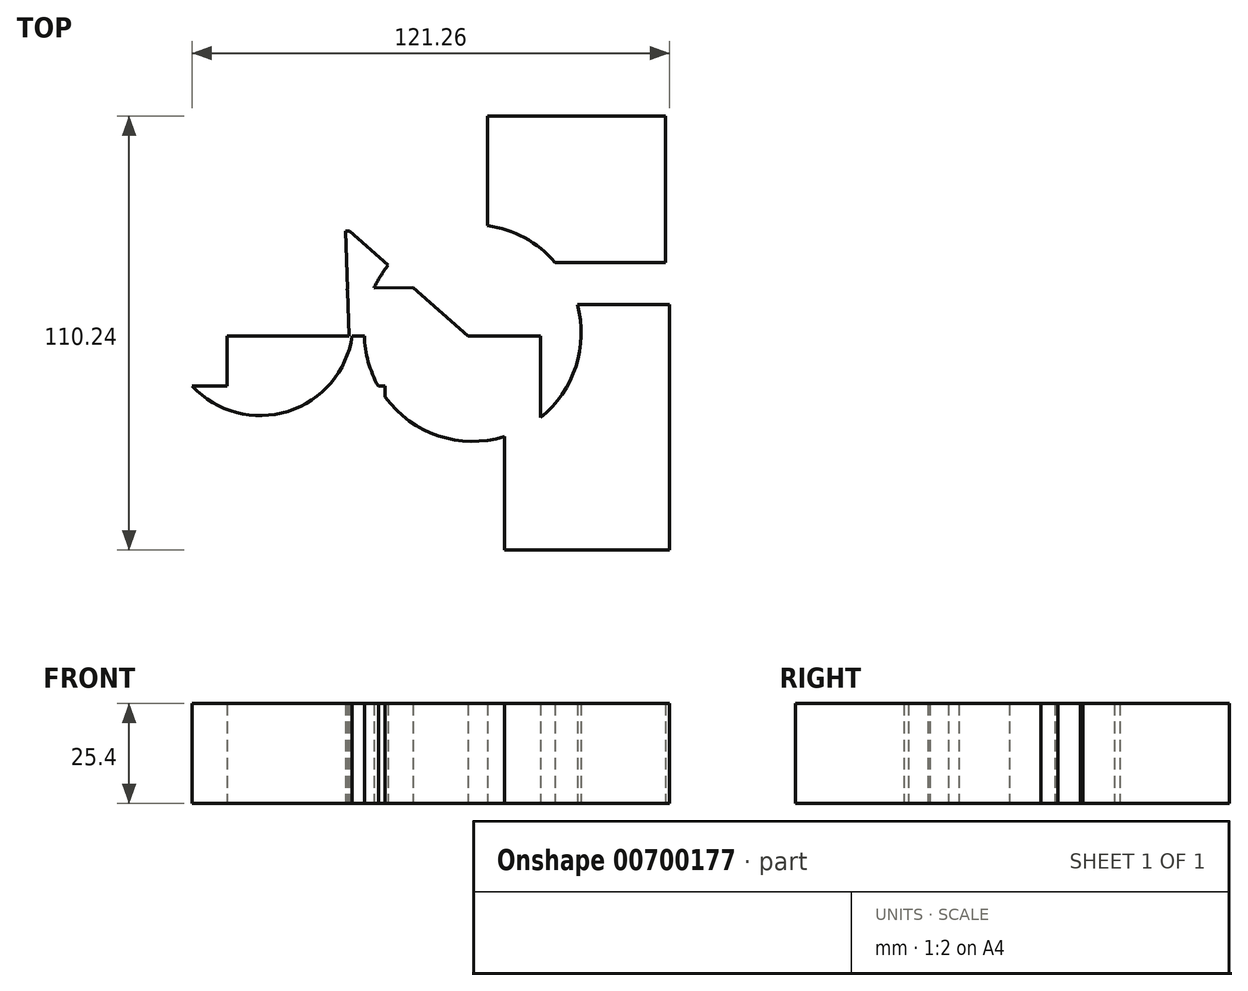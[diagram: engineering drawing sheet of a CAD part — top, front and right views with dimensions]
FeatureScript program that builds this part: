
annotation { "Feature Type Name" : "Feature", "Feature Type Description" : "" }
export const myFeature = defineFeature(function(context is Context, id is Id, definition is map)
    precondition{}
    {
        {
            var Q0;
            Q0=qCreatedBy(makeId("Top.planeOp"),FACE);
            var sketch = newSketch(context, id + "F0", { "sketchPlane" : qUnion([Q0])});
            skLineSegment(sketch, "E0.bottom", {"start": v(-22.83, 32.45) * mm, "end": v(-5.78, 32.45) * mm});
            skLineSegment(sketch, "E0.right", {"start": v(-5.78, 32.45) * mm, "end": v(-5.78, 62.5) * mm});
            skArc(sketch, "E1", {"start": v(30.4, 24.45) * mm, "mid": v(-14.8, -6.45) * mm, "end": v(36.07, 13.78) * mm});
            skLineSegment(sketch, "E2.bottom", {"start": v(17.51, -48.63) * mm, "end": v(59.47, -48.63) * mm});
            skLineSegment(sketch, "E2.top", {"start": v(36.07, 13.78) * mm, "end": v(59.47, 13.78) * mm});
            skLineSegment(sketch, "E2.left", {"start": v(17.51, -48.63) * mm, "end": v(17.51, -19.86) * mm});
            skLineSegment(sketch, "E2.right", {"start": v(59.47, -48.63) * mm, "end": v(59.47, 13.78) * mm});
            skLineSegment(sketch, "E3", {"start": v(-22.83, 32.45) * mm, "end": v(-21.42, -11.3) * mm});
            skLineSegment(sketch, "E4", {"start": v(-39.2, 50.05) * mm, "end": v(-5.78, 47.18) * mm});
            skArc(sketch, "E5", {"start": v(-62.4, -6.35) * mm, "mid": v(-25.36, -4.68) * mm, "end": v(-35.45, 31) * mm});
            skLineSegment(sketch, "E6.bottom", {"start": v(58.4, 61.6) * mm, "end": v(13.25, 61.6) * mm});
            skLineSegment(sketch, "E6.top", {"start": v(58.4, 24.45) * mm, "end": v(30.4, 24.45) * mm});
            skLineSegment(sketch, "E6.left", {"start": v(58.4, 61.6) * mm, "end": v(58.4, 24.45) * mm});
            skLineSegment(sketch, "E6.right", {"start": v(13.25, 61.6) * mm, "end": v(13.25, 24.45) * mm});
            skLineSegment(sketch, "E7.trimOffspring", {"start": v(13.25, 45.54) * mm, "end": v(35.3, 43.65) * mm});
            skLineSegment(sketch, "E8.bottom", {"start": v(-63.74, -55.92) * mm, "end": v(-12.71, -55.92) * mm});
            skLineSegment(sketch, "E8.top", {"start": v(-63.74, -7.02) * mm, "end": v(-12.71, -7.02) * mm});
            skLineSegment(sketch, "E8.left", {"start": v(-63.74, -55.92) * mm, "end": v(-63.74, -7.02) * mm});
            skLineSegment(sketch, "E8.right", {"start": v(-12.71, -9.77) * mm, "end": v(-12.71, -7.02) * mm});
            skLineSegment(sketch, "E9.bottom", {"start": v(-52.9, -38.5) * mm, "end": v(26.76, -38.5) * mm});
            skLineSegment(sketch, "E9.top", {"start": v(-52.9, 5.78) * mm, "end": v(26.76, 5.78) * mm});
            skLineSegment(sketch, "E9.left", {"start": v(-52.9, -38.5) * mm, "end": v(-52.9, 5.78) * mm});
            skLineSegment(sketch, "E9.right", {"start": v(26.76, -38.5) * mm, "end": v(26.76, 5.78) * mm});
            skLineSegment(sketch, "E10", {"start": v(-50.05, 57.52) * mm, "end": v(47.56, -29.07) * mm});
            skLineSegment(sketch, "E11", {"start": v(47.2, 19.3) * mm, "end": v(-54.85, 16.98) * mm});
            skSolve(sketch);
        }
        {
            var Q0;
            {var subQ1=sQuery(id+"F0.wireOp",EDGE,"E6.bottom");Q0=makeQuery(id+"F0.imprint","IMPRINT",FACE,{"disambiguationData":[TD([[makeQuery(id+"F0.imprint","IMPRINT",EDGE,{"derivedFrom":subQ1}),1.0]])]});}
            var Q1;
            {var subQ0=sQuery(id+"F0.wireOp",EDGE,"E11");var subQ1=sQuery(id+"F0.wireOp",EDGE,"E3");var subQ2=makeQuery(id+"F0.imprint","INTERSECT",VERTEX,{"derivedFrom":[subQ1,subQ0]});Q1=makeQuery(id+"F0.imprint","IMPRINT",FACE,{"disambiguationData":[TD([[makeQuery(id+"F0.imprint","IMPRINT",EDGE,{"disambiguationData":[TD([[subQ2,-1.0]])],"derivedFrom":subQ1}),-1.0]])]});}
            var Q2;
            {var subQ0=sQuery(id+"F0.wireOp",EDGE,"E8.top");var subQ1=sQuery(id+"F0.wireOp",EDGE,"E5");var subQ2=makeQuery(id+"F0.imprint","INTERSECT",VERTEX,{"disambiguationData":[OD(0.0)],"derivedFrom":[subQ1,subQ0]});Q2=makeQuery(id+"F0.imprint","IMPRINT",FACE,{"disambiguationData":[TD([[makeQuery(id+"F0.imprint","IMPRINT",EDGE,{"disambiguationData":[TD([[subQ2,-1.0]])],"derivedFrom":subQ1}),1.0]])]});}
            var Q3;
            {var subQ0=sQuery(id+"F0.wireOp",EDGE,"E9.right");var subQ1=sQuery(id+"F0.wireOp",EDGE,"E9.top");var subQ2=makeQuery(id+"F0.imprint","INTERSECT",VERTEX,{"derivedFrom":[subQ1,subQ0]});Q3=makeQuery(id+"F0.imprint","IMPRINT",FACE,{"disambiguationData":[TD([[makeQuery(id+"F0.imprint","IMPRINT",EDGE,{"disambiguationData":[TD([[subQ2,1.0]])],"derivedFrom":subQ1}),-1.0]])]});}
            var Q4;
            {var subQ5=sQuery(id+"F0.wireOp",EDGE,"E0.bottom");var subQ7=sQuery(id+"F0.wireOp",EDGE,"E3");var subQ8=makeQuery(id+"F0.imprint","INTERSECT",VERTEX,{"derivedFrom":[subQ5,subQ7]});Q4=makeQuery(id+"F0.imprint","IMPRINT",FACE,{"disambiguationData":[TD([[makeQuery(id+"F0.imprint","IMPRINT",EDGE,{"disambiguationData":[TD([[subQ8,-1.0]])],"derivedFrom":subQ5}),-1.0]])]});}
            var Q5;
            {var subQ0=sQuery(id+"F0.wireOp",EDGE,"E10");var subQ1=sQuery(id+"F0.wireOp",EDGE,"E1");var subQ2=makeQuery(id+"F0.imprint","INTERSECT",VERTEX,{"disambiguationData":[OD(0.0)],"derivedFrom":[subQ1,subQ0]});Q5=makeQuery(id+"F0.imprint","IMPRINT",FACE,{"disambiguationData":[TD([[makeQuery(id+"F0.imprint","IMPRINT",EDGE,{"disambiguationData":[TD([[subQ2,-1.0]])],"derivedFrom":subQ1}),1.0]])]});}
            var Q6;
            {var subQ1=sQuery(id+"F0.wireOp",EDGE,"E2.bottom");Q6=makeQuery(id+"F0.imprint","IMPRINT",FACE,{"disambiguationData":[TD([[makeQuery(id+"F0.imprint","IMPRINT",EDGE,{"derivedFrom":subQ1}),1.0]])]});}
            var Q7;
            {var subQ0=sQuery(id+"F0.wireOp",EDGE,"E10");var subQ1=sQuery(id+"F0.wireOp",EDGE,"E1");var subQ2=makeQuery(id+"F0.imprint","INTERSECT",VERTEX,{"disambiguationData":[OD(1.0)],"derivedFrom":[subQ1,subQ0]});Q7=makeQuery(id+"F0.imprint","IMPRINT",FACE,{"disambiguationData":[TD([[makeQuery(id+"F0.imprint","IMPRINT",EDGE,{"disambiguationData":[TD([[subQ2,1.0]])],"derivedFrom":subQ1}),1.0]])]});}
            var Q8;
            {var subQ0=sQuery(id+"F0.wireOp",EDGE,"E5");var subQ1=sQuery(id+"F0.wireOp",EDGE,"E3");var subQ2=makeQuery(id+"F0.imprint","INTERSECT",VERTEX,{"disambiguationData":[OD(0.0)],"derivedFrom":[subQ1,subQ0]});Q8=makeQuery(id+"F0.imprint","IMPRINT",FACE,{"disambiguationData":[TD([[makeQuery(id+"F0.imprint","IMPRINT",EDGE,{"disambiguationData":[TD([[subQ2,-1.0]])],"derivedFrom":subQ1}),1.0]])]});}
            var Q9;
            {var subQ0=sQuery(id+"F0.wireOp",EDGE,"E11");var subQ1=sQuery(id+"F0.wireOp",EDGE,"E1");var subQ2=makeQuery(id+"F0.imprint","INTERSECT",VERTEX,{"derivedFrom":[subQ1,subQ0]});Q9=makeQuery(id+"F0.imprint","IMPRINT",FACE,{"disambiguationData":[TD([[makeQuery(id+"F0.imprint","IMPRINT",EDGE,{"disambiguationData":[TD([[subQ2,-1.0]])],"derivedFrom":subQ1}),1.0]])]});}
            var Q10;
            {var subQ0=sQuery(id+"F0.wireOp",EDGE,"E2.left");var subQ1=sQuery(id+"F0.wireOp",EDGE,"E1");var subQ2=makeQuery(id+"F0.imprint","INTERSECT",VERTEX,{"derivedFrom":[subQ1,subQ0]});Q10=makeQuery(id+"F0.imprint","IMPRINT",FACE,{"disambiguationData":[TD([[makeQuery(id+"F0.imprint","IMPRINT",EDGE,{"disambiguationData":[TD([[subQ2,-1.0]])],"derivedFrom":subQ1}),-1.0]])]});}
            var Q11;
            {var subQ1=sQuery(id+"F0.wireOp",EDGE,"E9.top");var subQ3=sQuery(id+"F0.wireOp",EDGE,"E3");var subQ4=makeQuery(id+"F0.imprint","INTERSECT",VERTEX,{"derivedFrom":[subQ3,subQ1]});Q11=makeQuery(id+"F0.imprint","IMPRINT",FACE,{"disambiguationData":[TD([[makeQuery(id+"F0.imprint","IMPRINT",EDGE,{"disambiguationData":[TD([[subQ4,-1.0]])],"derivedFrom":subQ3}),-1.0]])]});}
            var Q12;
            {var subQ0=sQuery(id+"F0.wireOp",EDGE,"E9.top");var subQ1=sQuery(id+"F0.wireOp",EDGE,"E3");var subQ2=makeQuery(id+"F0.imprint","INTERSECT",VERTEX,{"derivedFrom":[subQ1,subQ0]});Q12=makeQuery(id+"F0.imprint","IMPRINT",FACE,{"disambiguationData":[TD([[makeQuery(id+"F0.imprint","IMPRINT",EDGE,{"disambiguationData":[TD([[subQ2,-1.0]])],"derivedFrom":subQ1}),1.0]])]});}
            var Q13;
            {var subQ0=sQuery(id+"F0.wireOp",EDGE,"E9.left");var subQ1=sQuery(id+"F0.wireOp",EDGE,"E5");var subQ2=makeQuery(id+"F0.imprint","INTERSECT",VERTEX,{"derivedFrom":[subQ1,subQ0]});Q13=makeQuery(id+"F0.imprint","IMPRINT",FACE,{"disambiguationData":[TD([[makeQuery(id+"F0.imprint","IMPRINT",EDGE,{"disambiguationData":[TD([[subQ2,-1.0]])],"derivedFrom":subQ1}),1.0]])]});}
            var Q14;
            {var subQ5=sQuery(id+"F0.wireOp",EDGE,"E1");var subQ7=sQuery(id+"F0.wireOp",EDGE,"E11");var subQ9=makeQuery(id+"F0.imprint","INTERSECT",VERTEX,{"derivedFrom":[subQ5,subQ7]});Q14=makeQuery(id+"F0.imprint","IMPRINT",FACE,{"disambiguationData":[TD([[makeQuery(id+"F0.imprint","IMPRINT",EDGE,{"disambiguationData":[TD([[subQ9,-1.0]])],"derivedFrom":subQ5}),-1.0]])]});}
            var Q15;
            {var subQ0=sQuery(id+"F0.wireOp",EDGE,"E8.right");Q15=makeQuery(id+"F0.imprint","IMPRINT",FACE,{"disambiguationData":[TD([[makeQuery(id+"F0.imprint","IMPRINT",EDGE,{"derivedFrom":subQ0}),-1.0]])]});}
            extrude(context, id + "F1", {"entities" : qUnion([Q0, Q1, Q2, Q3, Q4, Q5, Q6, Q7, Q8, Q9, Q10, Q11, Q12, Q13, Q14, Q15]), "depth" : 25.4 * mm, "offsetDistance" : 25.4 * mm});
        }
    });
